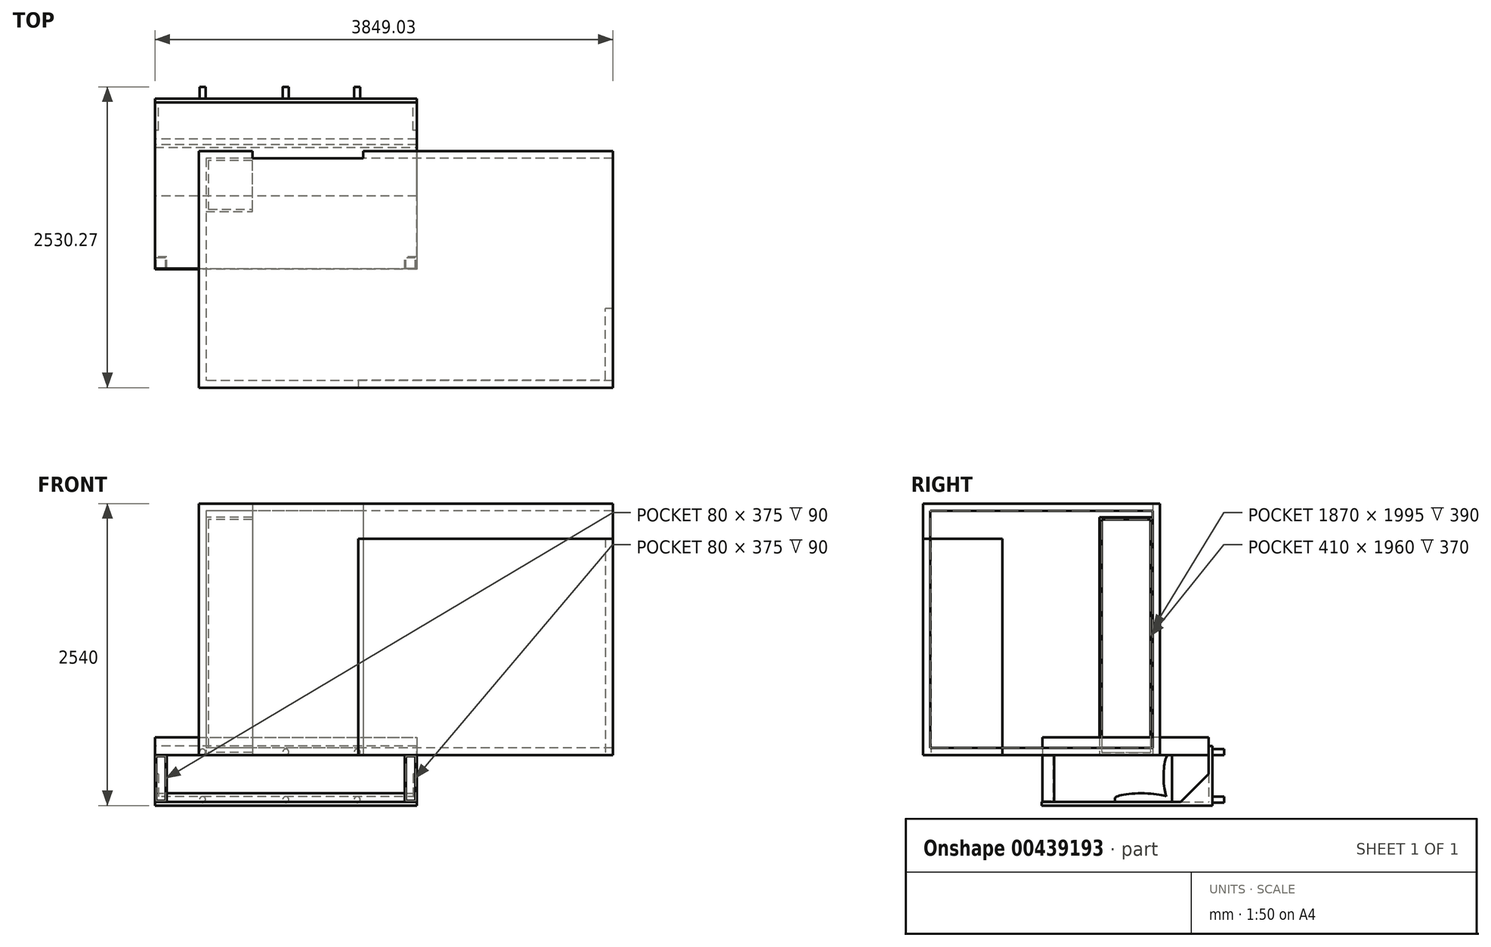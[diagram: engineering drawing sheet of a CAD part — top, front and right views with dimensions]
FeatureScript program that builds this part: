
annotation { "Feature Type Name" : "Feature", "Feature Type Description" : "" }
export const myFeature = defineFeature(function(context is Context, id is Id, definition is map)
    precondition{}
    {
        {
            var Q0;
            Q0=qCreatedBy(makeId("Top.planeOp"),FACE);
            var sketch = newSketch(context, id + "F0", { "sketchPlane" : qUnion([Q0])});
            skLineSegment(sketch, "E0.bottom", {"start": v(1740, 995) * mm, "end": v(-1740, 995) * mm});
            skLineSegment(sketch, "E0.top", {"start": v(1740, -995) * mm, "end": v(-1740, -995) * mm});
            skLineSegment(sketch, "E0.left", {"start": v(1740, 995) * mm, "end": v(1740, -995) * mm});
            skLineSegment(sketch, "E0.right", {"start": v(-1740, 995) * mm, "end": v(-1740, -995) * mm});
            skPoint(sketch, "E0.middle", {"position": v(0, 0) * mm});
            skSolve(sketch);
        }
        {
            var Q0;
            Q0 = qSketchRegion(id + "F0", true);
            extrude(context, id + "F1", {"entities" : qUnion([Q0]), "depth" : 2115 * mm});
        }
        {
            var Q0;
            Q0=makeQuery(id+"F1.opExtrude","SWEPT_FACE",FACE,{"disambiguationData":[OSD([sQuery(id+"F0.wireOp",EDGE,"E0.bottom")])]});
            cPlane(context, id + "F2", {"entities" : qUnion([Q0]), "cplaneType" : CPlaneType.OFFSET, "offset" : 0 * mm, "width" : 150 * mm, "height" : 150 * mm});
        }
        {
            var Q0;
            Q0=qCreatedBy(id+"F2.planeOp",FACE);
            var sketch = newSketch(context, id + "F3", { "sketchPlane" : qUnion([Q0])});
            skLineSegment(sketch, "E1.bottom", {"start": v(1290, 2115) * mm, "end": v(360, 2115) * mm});
            skLineSegment(sketch, "E1.top", {"start": v(1290, 0) * mm, "end": v(360, 0) * mm});
            skLineSegment(sketch, "E1.left", {"start": v(1290, 2115) * mm, "end": v(1290, 0) * mm});
            skLineSegment(sketch, "E1.right", {"start": v(360, 2115) * mm, "end": v(360, 0) * mm});
            skPoint(sketch, "E1.middle", {"position": v(825, 1057.5) * mm});
            skSolve(sketch);
        }
        {
            var Q0;
            Q0=makeQuery(id+"F1.opExtrude","SWEPT_FACE",FACE,{"disambiguationData":[OSD([sQuery(id+"F0.wireOp",EDGE,"E0.left")])]});
            shell(context, id + "F4", {"entities" : qUnion([Q0]), "thickness" : 60 * mm});
        }
        {
            var Q0;
            Q0=makeQuery(id+"F3.imprint","IMPRINT",FACE,{"disambiguationData":[TD([[makeQuery(id+"F3.imprint","IMPRINT",EDGE,{"derivedFrom":sQuery(id+"F3.wireOp",EDGE,"E1.bottom")}),1.0]])]});
            extrude(context, id + "F5", {"entities" : qUnion([Q0]), "operationType" : NewBodyOperationType.REMOVE, "oppositeDirection" : true, "depth" : 60 * mm});
        }
        {
            var Q0;
            Q0=qCreatedBy(makeId("Top.planeOp"),FACE);
            var sketch = newSketch(context, id + "F6", { "sketchPlane" : qUnion([Q0])});
            skLineSegment(sketch, "E2.bottom", {"start": v(-2109.03, 1405.27) * mm, "end": v(90.97, 1405.27) * mm});
            skLineSegment(sketch, "E2.top", {"start": v(-2109.03, 5.27) * mm, "end": v(90.97, 5.27) * mm});
            skLineSegment(sketch, "E2.left", {"start": v(-2109.03, 1405.27) * mm, "end": v(-2109.03, 5.27) * mm});
            skLineSegment(sketch, "E2.right", {"start": v(90.97, 1405.27) * mm, "end": v(90.97, 5.27) * mm});
            skPoint(sketch, "E2.middle", {"position": v(-1009.03, 705.27) * mm});
            skSolve(sketch);
        }
        {
            var Q0;
            Q0 = qSketchRegion(id + "F6", true);
            extrude(context, id + "F7", {"entities" : qUnion([Q0]), "depth" : 150 * mm});
        }
        {
            var Q0;
            Q0=makeQuery(id+"F7.opExtrude","SWEPT_FACE",FACE,{"disambiguationData":[OSD([sQuery(id+"F6.wireOp",EDGE,"E2.left")])]});
            cPlane(context, id + "F8", {"entities" : qUnion([Q0]), "cplaneType" : CPlaneType.OFFSET, "offset" : 0 * mm, "width" : 150 * mm, "height" : 150 * mm});
        }
        {
            var Q0;
            Q0=qCreatedBy(id+"F8.planeOp",FACE);
            var sketch = newSketch(context, id + "F9", { "sketchPlane" : qUnion([Q0])});
            skLineSegment(sketch, "E3.0", {"start": v(-1405.27, 150) * mm, "end": v(-1405.27, 0) * mm, "construction": true});
            skLineSegment(sketch, "E4.0", {"start": v(-1405.27, 0) * mm, "end": v(-5.27, 0) * mm, "construction": true});
            skLineSegment(sketch, "E5", {"start": v(-1405.27, 75) * mm, "end": v(-1435.27, 75) * mm});
            skLineSegment(sketch, "E6", {"start": v(-1435.27, 75) * mm, "end": v(-1435.27, -425) * mm});
            skLineSegment(sketch, "E7", {"start": v(-1435.27, -425) * mm, "end": v(0, -425) * mm});
            skLineSegment(sketch, "E8", {"start": v(0, -425) * mm, "end": v(0, -395) * mm});
            skLineSegment(sketch, "E9", {"start": v(0, -395) * mm, "end": v(-1170.27, -395) * mm});
            skLineSegment(sketch, "E10", {"start": v(-1405.27, -160) * mm, "end": v(-1405.27, 75) * mm});
            skLineSegment(sketch, "E11", {"start": v(-1405.27, -160) * mm, "end": v(-1170.27, -395) * mm});
            skPoint(sketch, "E12.orphan", {"position": v(-1405.27, -395) * mm});
            skLineSegment(sketch, "E13", {"start": v(-1405.27, -160) * mm, "end": v(-1405.27, -395) * mm});
            skLineSegment(sketch, "E14", {"start": v(-1170.27, -395) * mm, "end": v(-1405.27, -395) * mm});
            skSolve(sketch);
        }
        {
            var Q0;
            Q0=makeQuery(id+"F9.imprint","IMPRINT",FACE,{"disambiguationData":[TD([[makeQuery(id+"F9.imprint","IMPRINT",EDGE,{"derivedFrom":sQuery(id+"F9.wireOp",EDGE,"E5")}),1.0]])]});
            var Q1;
            Q1=makeQuery(id+"F9.imprint","IMPRINT",FACE,{"disambiguationData":[TD([[makeQuery(id+"F9.imprint","IMPRINT",EDGE,{"derivedFrom":sQuery(id+"F9.wireOp",EDGE,"E11")}),-1.0]])]});
            extrude(context, id + "F10", {"entities" : qUnion([Q0, Q1]), "oppositeDirection" : true, "depth" : 2200 * mm, "offsetDistance" : 25 * mm});
        }
        {
            var Q0;
            Q0=makeQuery(id+"F9.imprint","IMPRINT",FACE,{"disambiguationData":[TD([[makeQuery(id+"F9.imprint","IMPRINT",EDGE,{"derivedFrom":sQuery(id+"F9.wireOp",EDGE,"E11")}),-1.0]])]});
            extrude(context, id + "F11", {"entities" : qUnion([Q0]), "operationType" : NewBodyOperationType.REMOVE, "oppositeDirection" : true, "depth" : 2170 * mm});
        }
        {
            var Q0;
            Q0=makeQuery(id+"F9.imprint","IMPRINT",FACE,{"disambiguationData":[TD([[makeQuery(id+"F9.imprint","IMPRINT",EDGE,{"derivedFrom":sQuery(id+"F9.wireOp",EDGE,"E11")}),-1.0]])]});
            extrude(context, id + "F12", {"entities" : qUnion([Q0]), "operationType" : NewBodyOperationType.ADD, "oppositeDirection" : true, "depth" : 30 * mm});
        }
        {
            var Q0;
            Q0=makeQuery(id+"F10.opExtrude","SWEPT_FACE",FACE,{"disambiguationData":[OSD([sQuery(id+"F9.wireOp",EDGE,"E6")])]});
            cPlane(context, id + "F13", {"entities" : qUnion([Q0]), "cplaneType" : CPlaneType.OFFSET, "offset" : 0 * mm, "width" : 150 * mm, "height" : 150 * mm});
        }
        {
            var Q0;
            Q0=qCreatedBy(id+"F13.planeOp",FACE);
            var sketch = newSketch(context, id + "F14", { "sketchPlane" : qUnion([Q0])});
            skLineSegment(sketch, "E15.0.0", {"start": v(2109.03, -425) * mm, "end": v(2109.03, 75) * mm});
            skLineSegment(sketch, "E15.0.1", {"start": v(2109.03, 75) * mm, "end": v(-90.97, 75) * mm});
            skLineSegment(sketch, "E15.0.2", {"start": v(-90.97, 75) * mm, "end": v(-90.97, -425) * mm});
            skLineSegment(sketch, "E15.0.3", {"start": v(-90.97, -425) * mm, "end": v(2109.03, -425) * mm});
            skCircle(sketch, "E16", {"center": v(409.03, 25) * mm, "radius": 25 * mm});
            skCircle(sketch, "E17", {"center": v(1009.03, 25) * mm, "radius": 25 * mm});
            skCircle(sketch, "E18", {"center": v(1709.03, 25) * mm, "radius": 25 * mm});
            skCircle(sketch, "E19", {"center": v(409.03, -375) * mm, "radius": 25 * mm});
            skCircle(sketch, "E20", {"center": v(1009.03, -375) * mm, "radius": 25 * mm});
            skCircle(sketch, "E21", {"center": v(1709.03, -375) * mm, "radius": 25 * mm});
            skSolve(sketch);
        }
        {
            var Q0;
            Q0=makeQuery(id+"F14.imprint","IMPRINT",FACE,{"disambiguationData":[TD([[makeQuery(id+"F14.imprint","IMPRINT",EDGE,{"derivedFrom":sQuery(id+"F14.wireOp",EDGE,"E16")}),1.0]])]});
            var Q1;
            Q1=makeQuery(id+"F14.imprint","IMPRINT",FACE,{"disambiguationData":[TD([[makeQuery(id+"F14.imprint","IMPRINT",EDGE,{"derivedFrom":sQuery(id+"F14.wireOp",EDGE,"E18")}),1.0]])]});
            var Q2;
            Q2=makeQuery(id+"F14.imprint","IMPRINT",FACE,{"disambiguationData":[TD([[makeQuery(id+"F14.imprint","IMPRINT",EDGE,{"derivedFrom":sQuery(id+"F14.wireOp",EDGE,"E17")}),1.0]])]});
            var Q3;
            Q3=makeQuery(id+"F14.imprint","IMPRINT",FACE,{"disambiguationData":[TD([[makeQuery(id+"F14.imprint","IMPRINT",EDGE,{"derivedFrom":sQuery(id+"F14.wireOp",EDGE,"E19")}),1.0]])]});
            var Q4;
            Q4=makeQuery(id+"F14.imprint","IMPRINT",FACE,{"disambiguationData":[TD([[makeQuery(id+"F14.imprint","IMPRINT",EDGE,{"derivedFrom":sQuery(id+"F14.wireOp",EDGE,"E20")}),1.0]])]});
            var Q5;
            Q5=makeQuery(id+"F14.imprint","IMPRINT",FACE,{"disambiguationData":[TD([[makeQuery(id+"F14.imprint","IMPRINT",EDGE,{"derivedFrom":sQuery(id+"F14.wireOp",EDGE,"E21")}),1.0]])]});
            extrude(context, id + "F15", {"entities" : qUnion([Q0, Q1, Q2, Q3, Q4, Q5]), "operationType" : NewBodyOperationType.ADD, "depth" : 100 * mm, "offsetDistance" : 25 * mm});
        }
        {
            var Q0;
            Q0=makeQuery(id+"F7.opExtrude","SWEPT_FACE",FACE,{"disambiguationData":[OSD([sQuery(id+"F6.wireOp",EDGE,"E2.left")])]});
            cPlane(context, id + "F16", {"entities" : qUnion([Q0]), "cplaneType" : CPlaneType.OFFSET, "offset" : 0 * mm, "width" : 150 * mm, "height" : 150 * mm});
        }
        {
            var Q0;
            Q0=qCreatedBy(id+"F16.planeOp",FACE);
            var sketch = newSketch(context, id + "F17", { "sketchPlane" : qUnion([Q0])});
            skLineSegment(sketch, "E22.0.0", {"start": v(-1405.27, 0) * mm, "end": v(-5.27, 0) * mm});
            skLineSegment(sketch, "E22.0.1", {"start": v(-5.27, 0) * mm, "end": v(-5.27, 150) * mm});
            skLineSegment(sketch, "E22.0.2", {"start": v(-5.27, 150) * mm, "end": v(-1405.27, 150) * mm});
            skLineSegment(sketch, "E22.0.3", {"start": v(-1405.27, 150) * mm, "end": v(-1405.27, 0) * mm});
            skLineSegment(sketch, "E23.0", {"start": v(0, -395) * mm, "end": v(-1170.27, -395) * mm});
            skLineSegment(sketch, "E24.0", {"start": v(-1405.27, 75) * mm, "end": v(-1435.27, 75) * mm});
            skLineSegment(sketch, "E25", {"start": v(-1095.27, 0) * mm, "end": v(-1095.27, -395) * mm});
            skLineSegment(sketch, "E26", {"start": v(-1065.27, 0) * mm, "end": v(-1065.27, -365) * mm});
            skLineSegment(sketch, "E27", {"start": v(-1065.27, -365) * mm, "end": v(-615.27, -365) * mm});
            skLineSegment(sketch, "E28", {"start": v(-615.27, -365) * mm, "end": v(-615.27, -395) * mm});
            skEllipticalArc(sketch, "E29", {});
            skEllipticalArc(sketch, "E30", {});
            skLineSegment(sketch, "E31", {"start": v(-1048.94, -349.1) * mm, "end": v(-1065.27, -365) * mm});
            skLineSegment(sketch, "E32", {"start": v(-105.27, 0) * mm, "end": v(-105.27, -395) * mm});
            skLineSegment(sketch, "E33", {"start": v(-5.27, 0) * mm, "end": v(-5.27, -395) * mm});
            const initialGuessF17  = {"E29": [-1.0652677765488625, -0.1825, 0, 1, 0.1825, 0.04, 3.5620328245083903, 6.283185307179585], "E30": [-0.8402677765488625, -0.365, 1, 0, 0.225, 0.0425, 6.283185307179585, 2.75829870885337]};
            skSetInitialGuess(sketch, initialGuessF17);
            skSolve(sketch);
        }
        {
            var Q0;
            {var subQ1=sQuery(id+"F17.wireOp",EDGE,"E25");Q0=makeQuery(id+"F17.imprint","IMPRINT",FACE,{"disambiguationData":[TD([[makeQuery(id+"F17.imprint","IMPRINT",EDGE,{"derivedFrom":subQ1}),1.0]])]});}
            var Q1;
            Q1=makeQuery(id+"F17.imprint","IMPRINT",FACE,{"disambiguationData":[TD([[makeQuery(id+"F17.imprint","IMPRINT",EDGE,{"derivedFrom":sQuery(id+"F17.wireOp",EDGE,"E26")}),1.0]])]});
            var Q2;
            Q2=makeQuery(id+"F17.imprint","IMPRINT",FACE,{"disambiguationData":[TD([[makeQuery(id+"F17.imprint","IMPRINT",EDGE,{"derivedFrom":sQuery(id+"F17.wireOp",EDGE,"E27")}),1.0]])]});
            extrude(context, id + "F18", {"entities" : qUnion([Q0, Q1, Q2]), "oppositeDirection" : true, "depth" : 2200 * mm});
        }
        {
            var Q0;
            {var subQ2=sQuery(id+"F17.wireOp",EDGE,"E32");Q0=makeQuery(id+"F17.imprint","IMPRINT",FACE,{"disambiguationData":[TD([[makeQuery(id+"F17.imprint","IMPRINT",EDGE,{"derivedFrom":subQ2}),1.0]])]});}
            extrude(context, id + "F19", {"entities" : qUnion([Q0]), "oppositeDirection" : true, "depth" : 2200 * mm});
        }
        {
            var Q0;
            {var subQ2=sQuery(id+"F17.wireOp",EDGE,"E32");Q0=makeQuery(id+"F17.imprint","IMPRINT",FACE,{"disambiguationData":[TD([[makeQuery(id+"F17.imprint","IMPRINT",EDGE,{"derivedFrom":subQ2}),1.0]])]});}
            extrude(context, id + "F20", {"entities" : qUnion([Q0]), "operationType" : NewBodyOperationType.REMOVE, "oppositeDirection" : true, "depth" : 2100 * mm});
        }
        {
            var Q0;
            {var subQ2=sQuery(id+"F17.wireOp",EDGE,"E32");Q0=makeQuery(id+"F17.imprint","IMPRINT",FACE,{"disambiguationData":[TD([[makeQuery(id+"F17.imprint","IMPRINT",EDGE,{"derivedFrom":subQ2}),1.0]])]});}
            extrude(context, id + "F21", {"entities" : qUnion([Q0]), "oppositeDirection" : true, "depth" : 100 * mm});
        }
        {
            var Q0;
            Q0=makeQuery(id+"F19.opExtrude","SWEPT_FACE",FACE,{"disambiguationData":[OSD([sQuery(id+"F17.wireOp",EDGE,"E33")])]});
            var Q1;
            Q1=makeQuery(id+"F21.opExtrude","SWEPT_FACE",FACE,{"disambiguationData":[OSD([sQuery(id+"F17.wireOp",EDGE,"E33")])]});
            shell(context, id + "F22", {"entities" : qUnion([Q0, Q1]), "thickness" : 10 * mm});
        }
        {
            var Q0;
            Q0=qCreatedBy(makeId("Top.planeOp"),FACE);
            var sketch = newSketch(context, id + "F23", { "sketchPlane" : qUnion([Q0])});
            skLineSegment(sketch, "E34", {"start": v(-1290, 935) * mm, "end": v(-1680, 935) * mm});
            skLineSegment(sketch, "E35", {"start": v(-1680, 935) * mm, "end": v(-1680, 485) * mm});
            skLineSegment(sketch, "E36", {"start": v(-1680, 485) * mm, "end": v(-1290, 485) * mm});
            skLineSegment(sketch, "E37", {"start": v(-1290, 485) * mm, "end": v(-1290, 935) * mm});
            skSolve(sketch);
        }
        {
            var Q0;
            Q0 = qSketchRegion(id + "F23", true);
            extrude(context, id + "F24", {"entities" : qUnion([Q0]), "depth" : 2000 * mm});
        }
        {
            var Q0;
            Q0=makeQuery(id+"F24.opExtrude","SWEPT_FACE",FACE,{"disambiguationData":[OSD([sQuery(id+"F23.wireOp",EDGE,"E37")])]});
            shell(context, id + "F25", {"entities" : qUnion([Q0]), "thickness" : 20 * mm});
        }
        {
            var Q0;
            Q0=qCreatedBy(makeId("Top.planeOp"),FACE);
            var sketch = newSketch(context, id + "F26", { "sketchPlane" : qUnion([Q0])});
            skLineSegment(sketch, "E38.0.4", {"start": v(525, -995) * mm, "end": v(1740, -995) * mm});
            skLineSegment(sketch, "E38.0.5", {"start": v(1740, -995) * mm, "end": v(1740, -330) * mm});
            skLineSegment(sketch, "E39", {"start": v(1740, -330) * mm, "end": v(525, -330) * mm});
            skLineSegment(sketch, "E40", {"start": v(525, -330) * mm, "end": v(525, -930) * mm});
            skLineSegment(sketch, "E41", {"start": v(525, -930) * mm, "end": v(1675, -930) * mm});
            skLineSegment(sketch, "E42", {"start": v(1675, -930) * mm, "end": v(1675, -330) * mm});
            skLineSegment(sketch, "E43", {"start": v(525, -930) * mm, "end": v(-400, -930) * mm});
            skLineSegment(sketch, "E44", {"start": v(-400, -930) * mm, "end": v(-400, -995) * mm});
            skLineSegment(sketch, "E45", {"start": v(-400, -995) * mm, "end": v(525, -995) * mm});
            skLineSegment(sketch, "E46", {"start": v(765, -330) * mm, "end": v(765, -930) * mm});
            skSolve(sketch);
        }
        {
            var Q0;
            Q0=makeQuery(id+"F26.imprint","IMPRINT",FACE,{"disambiguationData":[TD([[makeQuery(id+"F26.imprint","IMPRINT",EDGE,{"derivedFrom":sQuery(id+"F26.wireOp",EDGE,"E38.0.4")}),1.0]])]});
            extrude(context, id + "F27", {"entities" : qUnion([Q0]), "depth" : 1820 * mm});
        }
    });
